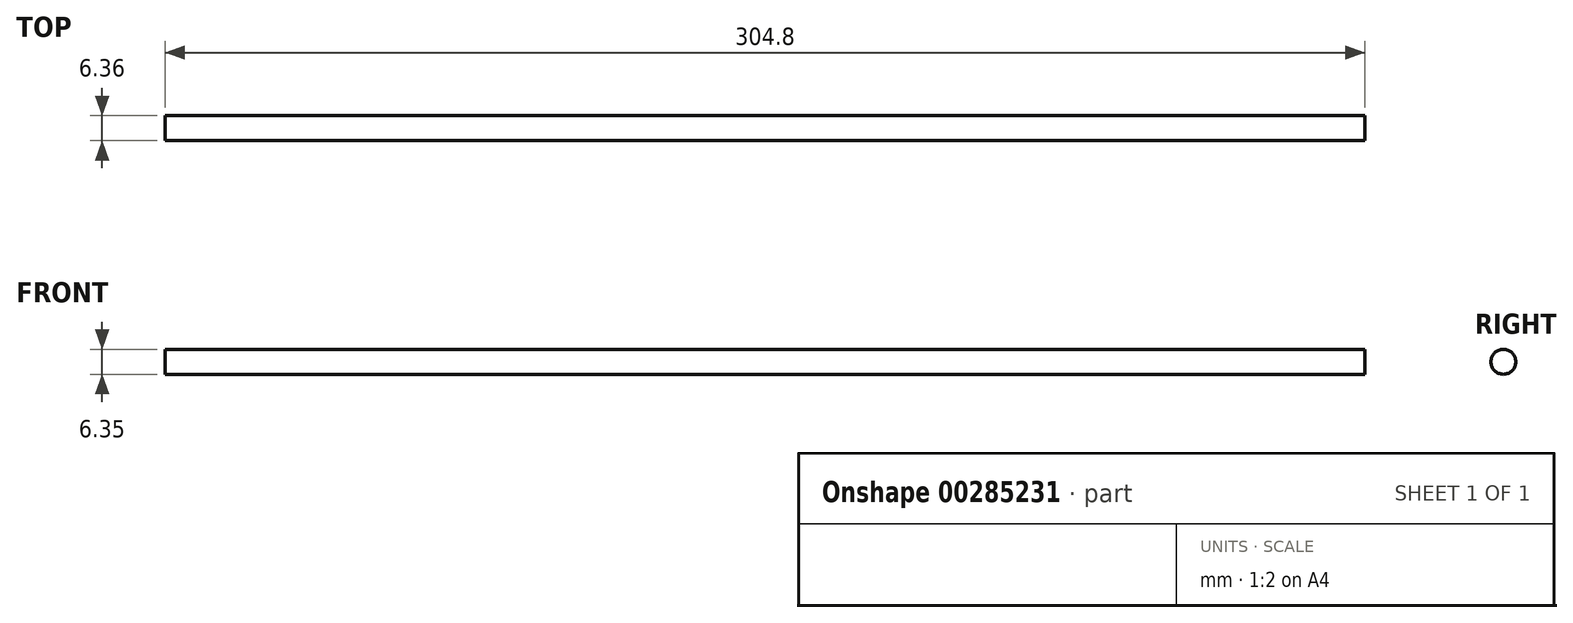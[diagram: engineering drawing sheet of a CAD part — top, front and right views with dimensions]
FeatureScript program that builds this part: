
annotation { "Feature Type Name" : "Feature", "Feature Type Description" : "" }
export const myFeature = defineFeature(function(context is Context, id is Id, definition is map)
    precondition{}
    {
        {
            var Q0;
            Q0=qCreatedBy(makeId("Front.planeOp"),FACE);
            var sketch = newSketch(context, id + "F0", { "sketchPlane" : qUnion([Q0])});
            skLineSegment(sketch, "E0.bottom", {"start": v(0, 0) * mm, "end": v(304.8, 0) * mm});
            skLineSegment(sketch, "E0.top", {"start": v(0, 3.18) * mm, "end": v(304.8, 3.18) * mm});
            skLineSegment(sketch, "E0.left", {"start": v(0, 0) * mm, "end": v(0, 3.18) * mm});
            skLineSegment(sketch, "E0.right", {"start": v(304.8, 0) * mm, "end": v(304.8, 3.18) * mm});
            skSolve(sketch);
        }
        {
            var Q0;
            Q0=makeQuery(id+"F0.imprint","IMPRINT",FACE,{"disambiguationData":[TD([[makeQuery(id+"F0.imprint","IMPRINT",EDGE,{"derivedFrom":sQuery(id+"F0.wireOp",EDGE,"E0.bottom")}),1.0]])]});
            var Q1;
            Q1=sQuery(id+"F0.wireOp",EDGE,"E0.top");
            revolve(context, id + "F1", {"entities" : qUnion([Q0]), "axis" : qUnion([Q1]), "revolveType" : RevolveType.FULL});
        }
    });
